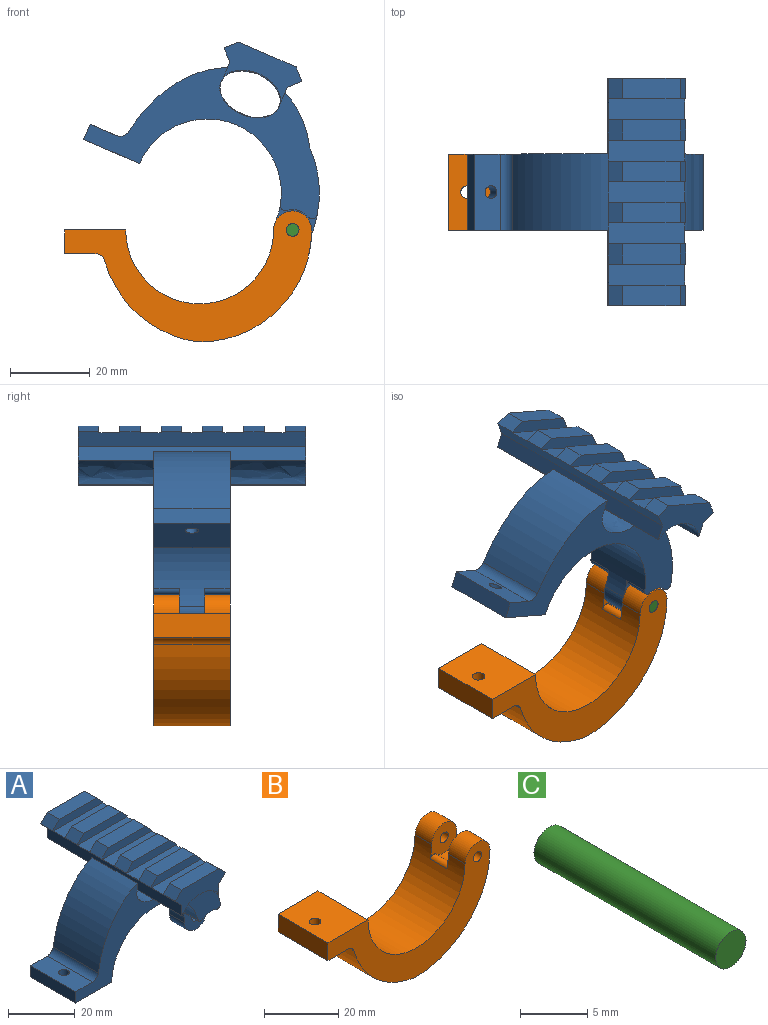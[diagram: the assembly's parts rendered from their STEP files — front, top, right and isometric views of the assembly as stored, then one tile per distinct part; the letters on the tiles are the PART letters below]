
ASSEMBLY  parts=3 mates=3
PART A: 65 faces, bbox 61.8x56.8x42.5 mm
  f0: plane 18.88x0.2mm, normal (0,0,-1), area 3.7mm2, adj f12,f21,f43,f46
  f1: plane 18.88x0.18mm, normal (0,0,-1), area 3.3mm2, adj f2,f20,f43,f45
  f2: plane 56.81x3.78mm, normal (-1,0,0), area 169.9mm2, adj f1,f3,f9,f20,f21,f44,f45,f46
  f3: plane 18.88x0.18mm, normal (0,0,-1), area 3.3mm2, adj f2,f21,f43,f46
  f4: plane 5.11x2.77mm, normal (-0.71,0,0.71), area 20mm2, adj f5,f9,f30,f35
  f5: plane 15.67x5.11mm, normal (0,0,1), area 80.1mm2, adj f4,f30,f35,f36
  f6: plane 5.11x2.77mm, normal (0.71,0,0.71), area 20mm2, adj f15,f24,f31,f32
  f7: plane 5.11x2.77mm, normal (-0.71,0,0.71), area 20mm2, adj f9,f19,f20,f34
  f8: plane 5.11x2.77mm, normal (-0.71,0,0.71), area 20mm2, adj f9,f24,f31,f32
  f9: plane 56.81x2.77mm, normal (-0.71,0,-0.71), area 214mm2, adj f2,f4,f7,f8,f10,f11,f20,f21
  f10: plane 5.11x2.77mm, normal (-0.71,0,0.71), area 20mm2, adj f9,f17,f21,f39
  f11: plane 5.11x2.77mm, normal (-0.71,0,0.71), area 20mm2, adj f9,f18,f38,f42
  f12: plane 56.81x3.78mm, normal (1,0,0), area 170.1mm2, adj f0,f13,f15,f20,f21,f45,f46,f64
  f13: plane 18.88x0.2mm, normal (0,0,-1), area 3.7mm2, adj f12,f20,f43,f45
  f14: plane 5.11x2.77mm, normal (0.71,0,0.71), area 20mm2, adj f15,f19,f20,f34
  f15: plane 56.81x2.77mm, normal (0.71,0,-0.71), area 214mm2, adj f6,f12,f14,f16,f20,f21,f22,f23
  f16: plane 5.11x2.77mm, normal (0.71,0,0.71), area 20mm2, adj f15,f17,f21,f39
  f17: plane 15.67x5.11mm, normal (0,0,1), area 80.1mm2, adj f10,f16,f21,f39
  f18: plane 15.67x5.11mm, normal (0,0,1), area 80.1mm2, adj f11,f22,f38,f42
  f19: plane 15.67x5.11mm, normal (0,0,1), area 80.1mm2, adj f7,f14,f20,f34
  f20: plane 21.21x9.32mm, normal (0,-1,0), area 115.8mm2, adj f1,f2,f7,f9,f12,f13,f14,f15
  f21: plane 21.21x9.32mm, normal (0,1,0), area 115.8mm2, adj f0,f2,f3,f9,f10,f12,f15,f16
  f22: plane 5.11x2.77mm, normal (0.71,0,0.71), area 20mm2, adj f15,f18,f38,f42
  f23: plane 20.75x5.23mm, normal (0,0,1), area 108.5mm2, adj f9,f15,f24,f25
  f24: plane 21.21x3mm, normal (0,1,0), area 55.9mm2, adj f6,f8,f9,f15,f23,f32
  f25: plane 21.21x3mm, normal (0,-1,0), area 55.9mm2, adj f9,f15,f23,f26,f27,f28
  f26: plane 5.11x2.77mm, normal (-0.71,0,0.71), area 20mm2, adj f9,f25,f27,f41
  f27: plane 15.67x5.11mm, normal (0,0,1), area 80.1mm2, adj f25,f26,f28,f41
  f28: plane 5.11x2.77mm, normal (0.71,0,0.71), area 20mm2, adj f15,f25,f27,f41
  f29: plane 20.75x5.23mm, normal (0,0,1), area 108.5mm2, adj f9,f15,f30,f31
  f30: plane 21.21x3mm, normal (0,1,0), area 55.9mm2, adj f4,f5,f9,f15,f29,f36
  f31: plane 21.21x3mm, normal (0,-1,0), area 55.9mm2, adj f6,f8,f9,f15,f29,f32
  f32: plane 15.67x5.11mm, normal (0,0,1), area 80.1mm2, adj f6,f8,f24,f31
  f33: plane 20.75x5.23mm, normal (0,0,1), area 108.5mm2, adj f9,f15,f34,f35
  f34: plane 21.21x3mm, normal (0,1,0), area 55.9mm2, adj f7,f9,f14,f15,f19,f33
  f35: plane 21.21x3mm, normal (0,-1,0), area 55.9mm2, adj f4,f5,f9,f15,f33,f36
  f36: plane 5.11x2.77mm, normal (0.71,0,0.71), area 20mm2, adj f5,f15,f30,f35
  f37: plane 20.75x5.23mm, normal (0,0,1), area 108.5mm2, adj f9,f15,f38,f39
  f38: plane 21.21x3mm, normal (0,1,0), area 55.9mm2, adj f9,f11,f15,f18,f22,f37
  f39: plane 21.21x3mm, normal (0,-1,0), area 55.9mm2, adj f9,f10,f15,f16,f17,f37
  f40: plane 20.75x5.23mm, normal (0,0,1), area 108.5mm2, adj f9,f15,f41,f42
  f41: plane 21.21x3mm, normal (0,1,0), area 55.9mm2, adj f9,f15,f26,f27,f28,f40
  f42: plane 21.21x3mm, normal (0,-1,0), area 55.9mm2, adj f9,f11,f15,f18,f22,f40
  f43: extruded ~56.81x15.83mm, area 1501.5mm2, adj f0,f1,f3,f13,f20,f21,f45,f46
  f44: extruded ~24.68x19.05mm, area 588mm2, adj f2,f45,f46,f63
  f45: plane 61.16x30.79mm, normal (0,-1,0), area 616.3mm2, adj f1,f2,f12,f13,f43,f44,f47,f50
  f46: plane 61.16x30.79mm, normal (0,1,0), area 616.3mm2, adj f0,f2,f3,f12,f43,f44,f47,f50
  f47: cylinder r=28.03mm len=20.53mm, axis (0,-1,0), area 363.1mm2, adj f45,f46,f49,f55,f57,f59,f61,f64
  f48: cylinder r=1.59mm len=6.35mm, axis (0,-1,0), area 63.3mm2, adj f55,f57
  f49: cylinder r=4.76mm len=9.53mm, axis (0,-1,0), area 95mm2, adj f47,f50,f55,f57
  f50: cylinder r=18.5mm len=37mm, axis (0,-1,0), area 1048.9mm2, adj f45,f46,f49,f51,f55,f57,f60,f62
  f51: plane 19.05x15.24mm, normal (0,0,-1), area 282.4mm2, adj f45,f46,f50,f52,f58
  f52: plane 19.05x4.11mm, normal (-1,0,0), area 78.3mm2, adj f45,f46,f51,f53
  f53: plane 19.05x7.08mm, normal (0,0,1), area 126.9mm2, adj f45,f46,f52,f58,f63
  f54: cylinder r=5.08mm len=6.35mm, axis (0,1,0), area 37.9mm2, adj f46,f55,f61,f62
  f55: plane 10.69x10.09mm, normal (0,1,0), area 71.3mm2, adj f47,f48,f49,f50,f54,f61,f62
  f56: cylinder r=5.08mm len=6.35mm, axis (0,-1,0), area 37.9mm2, adj f45,f57,f59,f60
  f57: plane 10.69x10.09mm, normal (0,-1,0), area 71.3mm2, adj f47,f48,f49,f50,f56,f59,f60
  f58: cylinder r=1.59mm len=4.11mm, axis (0,0,1), area 41mm2, adj f51,f53
  f59: cylinder r=1.27mm len=6.35mm, axis (0,1,0), area 18.2mm2, adj f45,f47,f56,f57
  f60: cylinder r=1.27mm len=6.35mm, axis (0,-1,0), area 16.3mm2, adj f45,f50,f56,f57
  f61: cylinder r=1.27mm len=6.35mm, axis (0,1,0), area 18.2mm2, adj f46,f47,f54,f55
  f62: cylinder r=1.27mm len=6.35mm, axis (0,-1,0), area 16.3mm2, adj f46,f50,f54,f55
  f63: cylinder r=2.54mm len=19.05mm, axis (0,-1,0), area 65.5mm2, adj f44,f45,f46,f53
  f64: extruded ~19.05x11.23mm, area 294mm2, adj f12,f45,f46,f47
PART B: 26 faces, bbox 61.8x19.1x32.8 mm
  f0: cylinder r=1.59mm len=3.18mm, axis (0,0,1), area 31mm2, adj f11,f16
  f1: plane 61.77x32.79mm, normal (0,-1,0), area 692.8mm2, adj f2,f4,f5,f6,f11,f12,f13,f15
  f2: cylinder r=18.5mm len=37mm, axis (0,1,0), area 1078.1mm2, adj f1,f3,f5,f7,f8,f9,f11,f24
  f3: plane 10.69x10.09mm, normal (0,1,0), area 71.3mm2, adj f2,f4,f5,f6,f14,f23,f24
  f4: cylinder r=1.59mm len=6.35mm, axis (0,1,0), area 63.3mm2, adj f1,f3
  f5: cylinder r=4.76mm len=9.53mm, axis (0,1,0), area 95mm2, adj f1,f2,f3,f6
  f6: cylinder r=28.03mm len=28.49mm, axis (0,1,0), area 809.6mm2, adj f1,f3,f5,f7,f8,f9,f13,f23
  f7: plane 61.77x32.79mm, normal (0,1,0), area 692.8mm2, adj f2,f6,f9,f10,f11,f12,f13,f15
  f8: plane 10.69x10.09mm, normal (0,-1,0), area 71.3mm2, adj f2,f6,f9,f10,f14,f23,f24
  f9: cylinder r=4.76mm len=9.53mm, axis (0,-1,0), area 95mm2, adj f2,f6,f7,f8
  f10: cylinder r=1.59mm len=6.35mm, axis (0,-1,0), area 63.3mm2, adj f7,f8
  f11: plane 19.05x15.24mm, normal (0,0,1), area 282.4mm2, adj f0,f1,f2,f7,f12
  f12: plane 19.05x5.89mm, normal (-1,0,0), area 112.2mm2, adj f1,f7,f11,f15
  f13: cylinder r=28.29mm len=23.31mm, axis (0,-1,0), area 622.7mm2, adj f1,f6,f7,f25
  f14: cylinder r=5.08mm len=6.35mm, axis (0,1,0), area 37.9mm2, adj f3,f8,f23,f24
  f15: plane 19.05x7.53mm, normal (0,0,-1), area 117.2mm2, adj f1,f7,f12,f17,f18,f19,f20,f21
  f16: plane 6.35x5.5mm, normal (0,0,-1), area 18.3mm2, adj f0,f17,f18,f19,f20,f21,f22
  f17: plane 2.78x2.75mm, normal (0.5,-0.87,0), area 8.8mm2, adj f15,f16,f18,f22
  f18: plane 2.78x2.75mm, normal (-0.5,-0.87,0), area 8.8mm2, adj f15,f16,f17,f19
  f19: plane 3.18x2.78mm, normal (-1,0,0), area 8.8mm2, adj f15,f16,f18,f20
  f20: plane 2.78x2.75mm, normal (-0.5,0.87,0), area 8.8mm2, adj f15,f16,f19,f21
  f21: plane 2.78x2.75mm, normal (0.5,0.87,0), area 8.8mm2, adj f15,f16,f20,f22
  f22: plane 3.18x2.78mm, normal (1,0,0), area 8.8mm2, adj f15,f16,f17,f21
  f23: cylinder r=1.27mm len=6.35mm, axis (0,1,0), area 18.2mm2, adj f3,f6,f8,f14
  f24: cylinder r=1.27mm len=6.35mm, axis (0,-1,0), area 16.3mm2, adj f2,f3,f8,f14
  f25: cylinder r=2.54mm len=19.05mm, axis (0,-1,0), area 62.6mm2, adj f1,f7,f13,f15
PART C: 3 faces, bbox 3.2x19.1x3.2 mm
  f0: cylinder r=1.59mm len=19.05mm, axis (0,1,0), area 190mm2, adj f1,f2
  f1: plane 3.18x3.18mm, normal (0,-1,0), area 7.9mm2, adj f0
  f2: plane 3.18x3.18mm, normal (0,1,0), area 7.9mm2, adj f0
PLACE A rot(axis=(0,1,0),23.4deg) t=(1.92,0,-3.45)mm
PLACE B at identity fixed
PLACE C t=(70.75,19.05,-42.46)mm fixed
MATE planar A.f45 <-> B.f1  axis (0,-1,0) through (6.67,9.52,11.26)mm
MATE cylindrical A.f48 <-> C.f0  axis (0,-1,0) through (23.26,15.88,-12.7)mm
MATE cylindrical C.f0 <-> B.f4  axis (0,1,0) through (23.26,19.05,-12.7)mm
